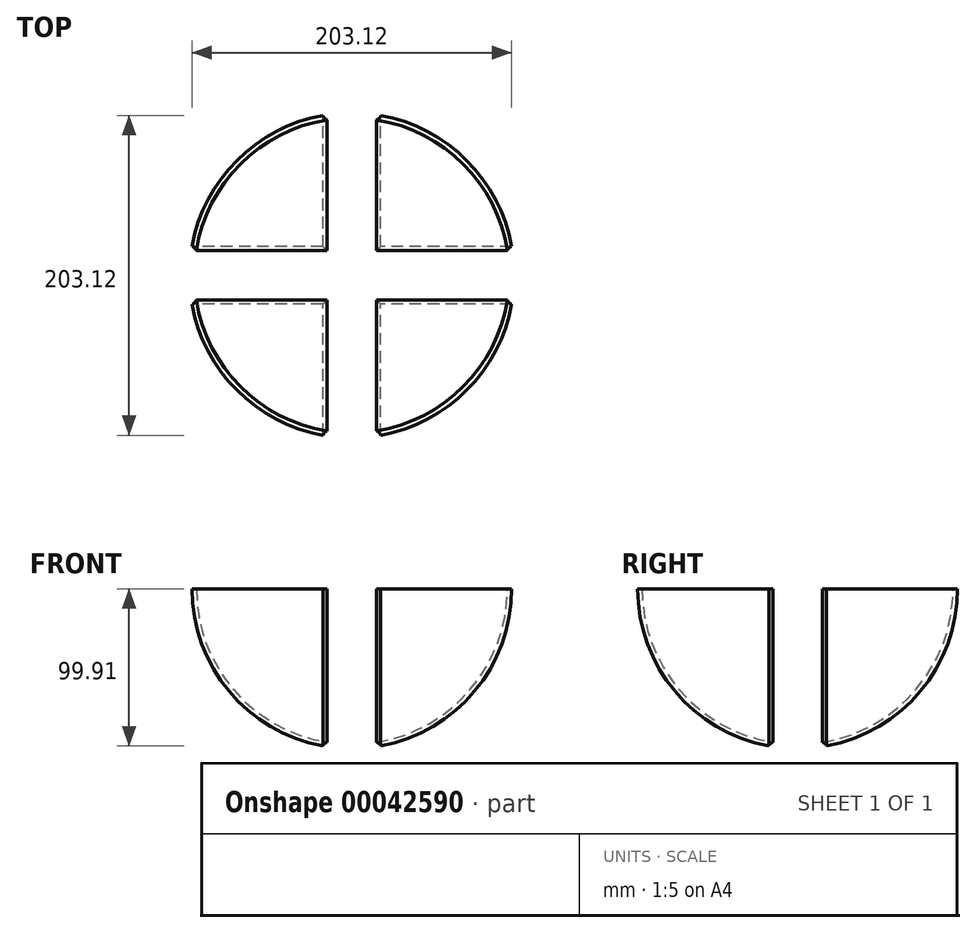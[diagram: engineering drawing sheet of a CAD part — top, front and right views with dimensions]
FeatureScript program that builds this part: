
annotation { "Feature Type Name" : "Feature", "Feature Type Description" : "" }
export const myFeature = defineFeature(function(context is Context, id is Id, definition is map)
    precondition{}
    {
        {
            var Q0;
            Q0=qCreatedBy(makeId("Top.planeOp"),FACE);
            var sketch = newSketch(context, id + "F0", { "sketchPlane" : qUnion([Q0])});
            skEllipse(sketch, "E0", {"center": v(-101.6, 0) * mm, "majorRadius": 19.05 * mm, "minorRadius": 6.35 * mm, "majorAxis": v(0, 1)});
            skFitSpline(sketch, "E1.0", {"points": [v(-101.44, 17.45) * mm, v(-101.6, 17.47) * mm, v(-101.76, 17.45) * mm, v(-102, 17.35) * mm, v(-102.36, 17.09) * mm, v(-102.79, 16.64) * mm, v(-103.24, 16) * mm, v(-103.87, 14.88) * mm, v(-104.6, 13.06) * mm, v(-105.23, 10.78) * mm, v(-105.65, 8.71) * mm, v(-105.99, 6.54) * mm, v(-106.22, 4.22) * mm, v(-106.34, 1.83) * mm, v(-106.37, 0) * mm, v(-106.34, -1.83) * mm, v(-106.22, -4.22) * mm, v(-105.99, -6.54) * mm, v(-105.65, -8.71) * mm, v(-105.23, -10.78) * mm, v(-104.6, -13.06) * mm, v(-103.87, -14.88) * mm, v(-103.24, -16) * mm, v(-102.79, -16.64) * mm, v(-102.36, -17.09) * mm, v(-102, -17.35) * mm, v(-101.76, -17.45) * mm, v(-101.6, -17.47) * mm, v(-101.44, -17.45) * mm, v(-101.2, -17.35) * mm, v(-100.84, -17.09) * mm, v(-100.41, -16.64) * mm, v(-99.96, -16) * mm, v(-99.33, -14.88) * mm, v(-98.6, -13.06) * mm, v(-97.97, -10.78) * mm, v(-97.55, -8.71) * mm, v(-97.21, -6.54) * mm, v(-96.98, -4.22) * mm, v(-96.86, -1.83) * mm, v(-96.83, 0) * mm, v(-96.86, 1.83) * mm, v(-96.98, 4.22) * mm, v(-97.21, 6.54) * mm, v(-97.55, 8.71) * mm, v(-97.97, 10.78) * mm, v(-98.6, 13.06) * mm, v(-99.33, 14.88) * mm, v(-99.96, 16) * mm, v(-100.41, 16.64) * mm, v(-100.84, 17.09) * mm, v(-101.2, 17.35) * mm, v(-101.44, 17.45) * mm, v(-101.6, 17.47) * mm, v(-101.76, 17.45) * mm, v(-101.44, 17.45) * mm]});
            skLineSegment(sketch, "E2", {"start": v(0, -50.53) * mm, "end": v(0, 55.5) * mm, "construction": true});
            skSolve(sketch);
        }
        {
            var Q0;
            Q0=sQuery(id+"F0.wireOp",EDGE,"E0");
            var Q1;
            Q1=sQuery(id+"F0.wireOp",EDGE,"E1.0");
            var Q2;
            Q2=sQuery(id+"F0.wireOp",EDGE,"E2");
            revolve(context, id + "F1", {"bodyType" : ToolBodyType.SURFACE, "surfaceEntities" : qUnion([Q0, Q1]), "axis" : qUnion([Q2]), "revolveType" : RevolveType.ONE_DIRECTION, "oppositeDirection" : true, "angle" : 180 * degree});
        }
        {
            var Q0;
            Q0=qCreatedBy(makeId("Top.planeOp"),FACE);
            var sketch = newSketch(context, id + "F2", { "sketchPlane" : qUnion([Q0])});
            skLineSegment(sketch, "E3", {"start": v(0, 0) * mm, "end": v(-43.66, 0) * mm, "construction": true});
            skEllipse(sketch, "E4", {"center": v(0, -101.6) * mm, "majorRadius": 19.05 * mm, "minorRadius": 6.35 * mm, "majorAxis": v(-1, 0)});
            skFitSpline(sketch, "E5.0", {"points": [v(-17.45, -101.44) * mm, v(-17.47, -101.6) * mm, v(-17.45, -101.76) * mm, v(-17.35, -102) * mm, v(-17.09, -102.36) * mm, v(-16.64, -102.79) * mm, v(-16, -103.24) * mm, v(-14.88, -103.87) * mm, v(-13.06, -104.6) * mm, v(-10.78, -105.23) * mm, v(-8.71, -105.65) * mm, v(-6.54, -105.99) * mm, v(-4.22, -106.22) * mm, v(-1.83, -106.34) * mm, v(0, -106.37) * mm, v(1.83, -106.34) * mm, v(4.22, -106.22) * mm, v(6.54, -105.99) * mm, v(8.71, -105.65) * mm, v(10.78, -105.23) * mm, v(13.06, -104.6) * mm, v(14.88, -103.87) * mm, v(16, -103.24) * mm, v(16.64, -102.79) * mm, v(17.09, -102.36) * mm, v(17.35, -102) * mm, v(17.45, -101.76) * mm, v(17.47, -101.6) * mm, v(17.45, -101.44) * mm, v(17.35, -101.2) * mm, v(17.09, -100.84) * mm, v(16.64, -100.41) * mm, v(16, -99.96) * mm, v(14.88, -99.33) * mm, v(13.06, -98.6) * mm, v(10.78, -97.97) * mm, v(8.71, -97.55) * mm, v(6.54, -97.21) * mm, v(4.22, -96.98) * mm, v(1.83, -96.86) * mm, v(0, -96.83) * mm, v(-1.83, -96.86) * mm, v(-4.22, -96.98) * mm, v(-6.54, -97.21) * mm, v(-8.71, -97.55) * mm, v(-10.78, -97.97) * mm, v(-13.06, -98.6) * mm, v(-14.88, -99.33) * mm, v(-16, -99.96) * mm, v(-16.64, -100.41) * mm, v(-17.09, -100.84) * mm, v(-17.35, -101.2) * mm, v(-17.45, -101.44) * mm, v(-17.47, -101.6) * mm, v(-17.45, -101.76) * mm, v(-17.45, -101.44) * mm]});
            skSolve(sketch);
        }
        {
            var Q0;
            Q0=sQuery(id+"F2.wireOp",EDGE,"E5.0");
            var Q1;
            Q1=sQuery(id+"F2.wireOp",EDGE,"E4");
            var Q2;
            Q2=sQuery(id+"F2.wireOp",EDGE,"E3");
            revolve(context, id + "F3", {"bodyType" : ToolBodyType.SURFACE, "surfaceEntities" : qUnion([Q0, Q1]), "axis" : qUnion([Q2]), "revolveType" : RevolveType.ONE_DIRECTION, "oppositeDirection" : true, "angle" : 180 * degree});
        }
        {
            var Q0;
            Q0=qCreatedBy(makeId("Right.planeOp"),FACE);
            var sketch = newSketch(context, id + "F4", { "sketchPlane" : qUnion([Q0])});
            skArc(sketch, "E6.0", {"start": v(-100.01, 0) * mm, "mid": v(-70.72, -70.72) * mm, "end": v(0, -100.01) * mm});
            skArc(sketch, "E7.0", {"start": v(-103.19, 0) * mm, "mid": v(-72.96, -72.96) * mm, "end": v(0, -103.19) * mm});
            skPoint(sketch, "E8.endSnap0", {"position": v(0, -101.6) * mm});
            skLineSegment(sketch, "E9", {"start": v(0, -101.6) * mm, "end": v(0, -100.01) * mm});
            skLineSegment(sketch, "E10", {"start": v(0, -100.01) * mm, "end": v(0, -103.19) * mm});
            skPoint(sketch, "E11.end.orphan", {"position": v(-101.6, 0) * mm});
            skLineSegment(sketch, "E12", {"start": v(-103.19, 0) * mm, "end": v(-100.01, 0) * mm});
            skLineSegment(sketch, "E13", {"start": v(0, -72.48) * mm, "end": v(0, 0) * mm});
            skSolve(sketch);
        }
        {
            var Q0;
            Q0 = qSketchRegion(id + "F4", true);
            var Q1;
            Q1=sQuery(id+"F4.wireOp",EDGE,"E13");
            revolve(context, id + "F5", {"entities" : qUnion([Q0]), "axis" : qUnion([Q1]), "revolveType" : RevolveType.FULL});
        }
        {
            var Q0;
            Q0=qCreatedBy(makeId("Top.planeOp"),FACE);
            var sketch = newSketch(context, id + "F6", { "sketchPlane" : qUnion([Q0])});
            skEllipse(sketch, "E14", {"center": v(-101.6, 0) * mm, "majorRadius": 18.26 * mm, "minorRadius": 5.56 * mm, "majorAxis": v(0, 1)});
            skLineSegment(sketch, "E15", {"start": v(0, 0) * mm, "end": v(0, 48.5) * mm});
            skSolve(sketch);
        }
        {
            var Q0;
            Q0 = qSketchRegion(id + "F6", true);
            var Q1;
            Q1=sQuery(id+"F6.wireOp",EDGE,"E15");
            revolve(context, id + "F7", {"operationType" : NewBodyOperationType.REMOVE, "entities" : qUnion([Q0]), "axis" : qUnion([Q1]), "revolveType" : RevolveType.FULL, "oppositeDirection" : true});
        }
        {
            var Q0;
            Q0=qCreatedBy(makeId("Top.planeOp"),FACE);
            var sketch = newSketch(context, id + "F8", { "sketchPlane" : qUnion([Q0])});
            skEllipse(sketch, "E16", {"center": v(0, 101.6) * mm, "majorRadius": 18.26 * mm, "minorRadius": 5.56 * mm, "majorAxis": v(1, 0)});
            skLineSegment(sketch, "E17", {"start": v(0, 0) * mm, "end": v(55.53, 0) * mm});
            skSolve(sketch);
        }
        {
            var Q0;
            Q0 = qSketchRegion(id + "F8", true);
            var Q1;
            Q1=sQuery(id+"F8.wireOp",EDGE,"E17");
            revolve(context, id + "F9", {"operationType" : NewBodyOperationType.REMOVE, "entities" : qUnion([Q0]), "axis" : qUnion([Q1]), "revolveType" : RevolveType.FULL, "oppositeDirection" : true});
        }
    });
